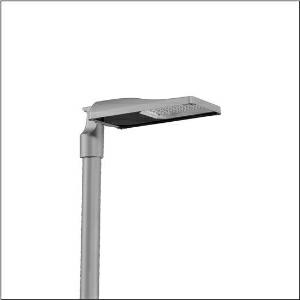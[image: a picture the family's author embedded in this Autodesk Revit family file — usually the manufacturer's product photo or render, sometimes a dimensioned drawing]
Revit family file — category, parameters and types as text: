
# Revit family: streetlight_sl_31_mini___st1_0a_5xh2d31a08ha_13ce
name_source: partatom
category: Lighting Fixtures
units: mm (PartAtom-declared; Revit-internal decimal feet)

## family parameters
Cut with Voids When Loaded = No
Host = Face
Light Source = No
Part Type = Normal
Room Calculation Point = No
Round Connector Dimension = Use Diameter
Shared = No

## types (1)
- --- (1 x LED, 9240 lm, 68.3 W, 3000K)
    Apparent Load = 68 VA
    CIE Flux Codes = 37 72 97 100 100
    Color Rendering = 70
    Color Temperature = 3000K
    Default Elevation = 1800 mm
    Description = Streetlight SL 31 mini Easy, Desk-Remote mast luminaire for post-top, side-entry; light control with lens of PMMA; light distribution: ST1.0a, direct asymmetric distribution, for standard-compliant lighting for roads and squares; LED: luminous flux: 9.240lm, light colour: 730, colour temperature: 3000K; luminous efficacy: 135,3lm/W; control: pre-setting: linear dimming characteristic, flexible luminous flux parameterisation, time-dependent luminous flux control, constant luminous flux control, intelligent temperature release in ECG and LED module, overheat protection; luminaire housing, of diecast aluminium, SITECO metallic grey (DB 702S), corrosivity category C5 high according to DIN EN ISO 12944; cover of toughened safety glass, transparent, mast flange of diecast aluminium, SITECO metallic grey (DB 702S), spigot size: 76/60mm, mast flange included unmounted; with cable H07RN-F 2x 1.5mm², cable length: 8,5m, connection cable pre-assembled; mains connection: 220..240V, AC, 50/60Hz; power consumption (at start of service life): 68,3W / (at end of service life): 74,8W / (with reduced operation 50%): 29,7W; protection rating (complete): IP66; insulation class (complete): insulation class II (safety insulation); impact resistance: IK10; certification: CE, ENEC, ENEC+, VDE, UKCA; permissible operating ambient temperature for outdoor applications: -40..+50°C; packaging unit: 1 piece

Light Distribution: ST1.0a
    Height = 76 mm
    Lamp = 1 x LED
    Lamp Light Flux = 9240 lm
    Lamp Power = 68.3 W
    Lamp count = 1
    Length = 547 mm
    Luminous efficacy = 135 lm/W
    Manufacturer = Siteco
    ModVariant = No
    Model = 5XH2D31A08HA
    Number of Poles = 1
    OnlyDefault = Yes
    Power Factor = 1
    Product Name = Streetlight SL 31 mini | ST1.0a
    Product group = mast luminaire | pylon top
    ProductGroupID = 6100
    Protection Class = Protection class II
    Protection Degree = IP 66
    RLX_Detail_Level = 1
    RLX_Emergency_Light_Flux = 0 lm
    RLX_Emergency_Type = 0
    RLX_Emergency_Type_DB = No
    RlxData = <blob elided: 39457 chars, md5=8f17ffae>
    Socket = socket
    Standby Power = 0 W
    System Light Flux = 9240 lm
    System Power = 68 W
    Type Comments = factory setting: luminous flux: 100 % | dim-lin: 254 | 693 mA
    Type Image = l_1300326.jpg
    URL = http://relux.com
    VarID = @adj_061807
    Voltage = 0 V
    Weight = 0.00 kg
    Width = 265 mm

## geometry (parser evidence)
native form markers: Blend x4, Sweep x9
no freeform markers — native parametric forms only
